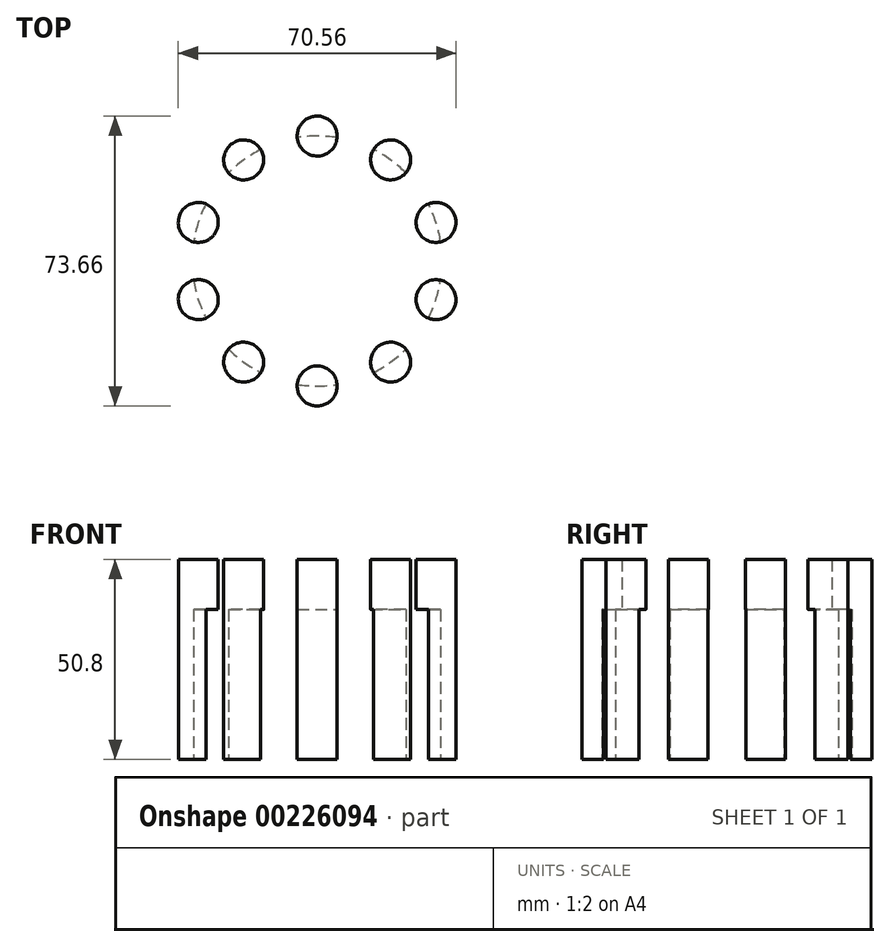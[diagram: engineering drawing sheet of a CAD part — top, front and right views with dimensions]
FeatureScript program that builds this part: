
annotation { "Feature Type Name" : "Feature", "Feature Type Description" : "" }
export const myFeature = defineFeature(function(context is Context, id is Id, definition is map)
    precondition{}
    {
        {
            var Q0;
            Q0=qCreatedBy(makeId("Top.planeOp"),FACE);
            var sketch = newSketch(context, id + "F0", { "sketchPlane" : qUnion([Q0])});
            skCircle(sketch, "E0", {"center": v(0, 0) * mm, "radius": 31.75 * mm});
            skSolve(sketch);
        }
        {
            var Q0;
            Q0=makeQuery(id+"F0.imprint","IMPRINT",FACE,{"disambiguationData":[TD([[makeQuery(id+"F0.imprint","IMPRINT",EDGE,{"derivedFrom":sQuery(id+"F0.wireOp",EDGE,"E0")}),1.0]])]});
            extrude(context, id + "F1", {"entities" : qUnion([Q0]), "depth" : 38.1 * mm});
        }
        {
            var Q0;
            Q0=qCreatedBy(makeId("Top.planeOp"),FACE);
            var sketch = newSketch(context, id + "F2", { "sketchPlane" : qUnion([Q0])});
            skCircle(sketch, "E1", {"center": v(0, 31.75) * mm, "radius": 5.08 * mm});
            skCircle(sketch, "E2.1.0", {"center": v(-18.66, 25.69) * mm, "radius": 5.08 * mm});
            skCircle(sketch, "E2.2.0", {"center": v(-30.2, 9.81) * mm, "radius": 5.08 * mm});
            skCircle(sketch, "E2.3.0", {"center": v(-30.2, -9.81) * mm, "radius": 5.08 * mm});
            skCircle(sketch, "E2.4.0", {"center": v(-18.66, -25.69) * mm, "radius": 5.08 * mm});
            skCircle(sketch, "E2.5.0", {"center": v(0, -31.75) * mm, "radius": 5.08 * mm});
            skCircle(sketch, "E2.6.0", {"center": v(18.66, -25.69) * mm, "radius": 5.08 * mm});
            skCircle(sketch, "E2.7.0", {"center": v(30.2, -9.81) * mm, "radius": 5.08 * mm});
            skCircle(sketch, "E2.8.0", {"center": v(30.2, 9.81) * mm, "radius": 5.08 * mm});
            skCircle(sketch, "E2.9.0", {"center": v(18.66, 25.69) * mm, "radius": 5.08 * mm});
            skPoint(sketch, "E2.center", {"position": v(0, 0) * mm});
            skSolve(sketch);
        }
        {
            var Q0;
            Q0=qSketchRegion(id+"F2",true);
            extrude(context, id + "F3", {"entities" : qUnion([Q0]), "depth" : 50.8 * mm});
        }
        {
            var Q0;
            Q0=makeQuery(id+"F1.opExtrude","SWEPT_BODY",BODY,{"disambiguationData":[OSD([sQuery(id+"F0.wireOp",EDGE,"E0")])]});
            var Q1;
            Q1=makeQuery(id+"F3.opExtrude","SWEPT_BODY",BODY,{"disambiguationData":[OSD([sQuery(id+"F2.wireOp",EDGE,"E2.2.0")])]});
            var Q2;
            Q2=makeQuery(id+"F3.opExtrude","SWEPT_BODY",BODY,{"disambiguationData":[OSD([sQuery(id+"F2.wireOp",EDGE,"E2.3.0")])]});
            var Q3;
            Q3=makeQuery(id+"F3.opExtrude","SWEPT_BODY",BODY,{"disambiguationData":[OSD([sQuery(id+"F2.wireOp",EDGE,"E2.4.0")])]});
            var Q4;
            Q4=makeQuery(id+"F3.opExtrude","SWEPT_BODY",BODY,{"disambiguationData":[OSD([sQuery(id+"F2.wireOp",EDGE,"E2.5.0")])]});
            var Q5;
            Q5=makeQuery(id+"F3.opExtrude","SWEPT_BODY",BODY,{"disambiguationData":[OSD([sQuery(id+"F2.wireOp",EDGE,"E2.6.0")])]});
            var Q6;
            Q6=makeQuery(id+"F3.opExtrude","SWEPT_BODY",BODY,{"disambiguationData":[OSD([sQuery(id+"F2.wireOp",EDGE,"E2.7.0")])]});
            var Q7;
            Q7=makeQuery(id+"F3.opExtrude","SWEPT_BODY",BODY,{"disambiguationData":[OSD([sQuery(id+"F2.wireOp",EDGE,"E2.8.0")])]});
            var Q8;
            Q8=makeQuery(id+"F3.opExtrude","SWEPT_BODY",BODY,{"disambiguationData":[OSD([sQuery(id+"F2.wireOp",EDGE,"E2.9.0")])]});
            var Q9;
            Q9=makeQuery(id+"F3.opExtrude","SWEPT_BODY",BODY,{"disambiguationData":[OSD([sQuery(id+"F2.wireOp",EDGE,"E1")])]});
            var Q10;
            Q10=makeQuery(id+"F3.opExtrude","SWEPT_BODY",BODY,{"disambiguationData":[OSD([sQuery(id+"F2.wireOp",EDGE,"E2.1.0")])]});
            booleanBodies(context, id + "F4", {"operationType" : BooleanOperationType.SUBTRACTION, "tools" : qUnion([Q0]), "targets" : qUnion([Q1, Q2, Q3, Q4, Q5, Q6, Q7, Q8, Q9, Q10])});
        }
    });
